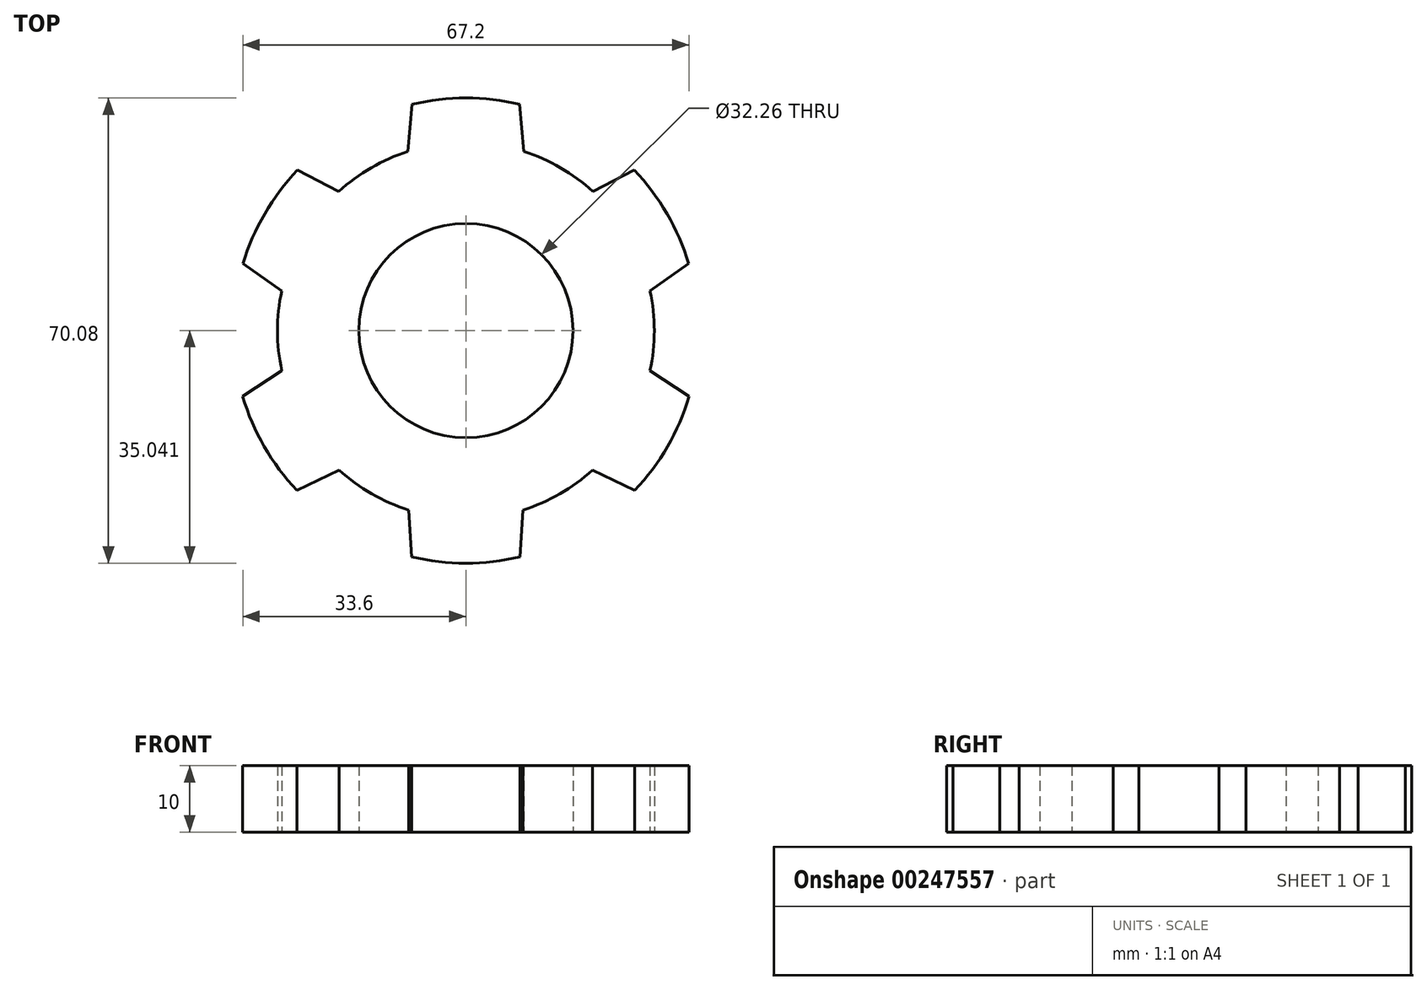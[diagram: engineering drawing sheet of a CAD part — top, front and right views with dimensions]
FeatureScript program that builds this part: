
annotation { "Feature Type Name" : "Feature", "Feature Type Description" : "" }
export const myFeature = defineFeature(function(context is Context, id is Id, definition is map)
    precondition{}
    {
        {
            var Q0;
            Q0=qCreatedBy(makeId("Top.planeOp"),FACE);
            var sketch = newSketch(context, id + "F0", { "sketchPlane" : qUnion([Q0])});
            skArc(sketch, "E0", {"start": v(-8.74, -1.22) * mm, "mid": v(-14.26, -3.69) * mm, "end": v(-19.13, -7.26) * mm});
            skArc(sketch, "E1", {"start": v(0, -63.26) * mm, "mid": v(4.11, -63.02) * mm, "end": v(8.17, -62.3) * mm});
            skLineSegment(sketch, "E2", {"start": v(8.1, 5.87) * mm, "end": v(8.74, -1.22) * mm});
            skLineSegment(sketch, "E3", {"start": v(25.36, -4.03) * mm, "end": v(19.13, -7.26) * mm});
            skLineSegment(sketch, "E4", {"start": v(33.56, -18.15) * mm, "end": v(27.74, -22.23) * mm});
            skLineSegment(sketch, "E5", {"start": v(33.6, -38.15) * mm, "end": v(27.72, -34.26) * mm});
            skPoint(sketch, "E6", {"position": v(25.45, -52.3) * mm});
            skPoint(sketch, "E7", {"position": v(19.08, -49.22) * mm});
            skLineSegment(sketch, "E8", {"start": v(19.08, -49.22) * mm, "end": v(25.45, -52.3) * mm});
            skLineSegment(sketch, "E9", {"start": v(8.62, -55.25) * mm, "end": v(8.17, -62.3) * mm});
            skArc(sketch, "E10.trimOffspring", {"start": v(8.1, 5.87) * mm, "mid": v(4.08, 6.58) * mm, "end": v(0, 6.82) * mm});
            skArc(sketch, "E11.trimOffspring", {"start": v(33.56, -18.15) * mm, "mid": v(30.3, -10.6) * mm, "end": v(25.36, -4.03) * mm});
            skArc(sketch, "E12.trimOffspring", {"start": v(25.45, -52.3) * mm, "mid": v(30.36, -45.71) * mm, "end": v(33.6, -38.15) * mm});
            skLineSegment(sketch, "E13.MirrorCS", {"start": v(-25.36, -4.03) * mm, "end": v(-19.13, -7.26) * mm});
            skPoint(sketch, "E14.MirrorP", {"position": v(-19.08, -49.22) * mm});
            skLineSegment(sketch, "E15.MirrorCS", {"start": v(-33.6, -38.15) * mm, "end": v(-27.72, -34.26) * mm});
            skPoint(sketch, "E16.MirrorP", {"position": v(-25.45, -52.3) * mm});
            skArc(sketch, "E17.MirrorCS", {"start": v(-25.45, -52.3) * mm, "mid": v(-30.36, -45.71) * mm, "end": v(-33.6, -38.15) * mm});
            skLineSegment(sketch, "E18.MirrorCS", {"start": v(-19.08, -49.22) * mm, "end": v(-25.45, -52.3) * mm});
            skLineSegment(sketch, "E19.MirrorCS", {"start": v(-8.1, 5.87) * mm, "end": v(-8.74, -1.22) * mm});
            skArc(sketch, "E20.MirrorCS", {"start": v(-33.56, -18.15) * mm, "mid": v(-30.3, -10.6) * mm, "end": v(-25.36, -4.03) * mm});
            skLineSegment(sketch, "E21.MirrorCS", {"start": v(-33.56, -18.15) * mm, "end": v(-27.74, -22.23) * mm});
            skLineSegment(sketch, "E22.MirrorCS", {"start": v(-8.62, -55.25) * mm, "end": v(-8.17, -62.3) * mm});
            skArc(sketch, "E23.MirrorC", {"start": v(8.74, -1.22) * mm, "mid": v(14.26, -3.69) * mm, "end": v(19.13, -7.26) * mm});
            skArc(sketch, "E24.MirrorCS", {"start": v(0, -63.26) * mm, "mid": v(-4.11, -63.02) * mm, "end": v(-8.17, -62.3) * mm});
            skArc(sketch, "E25.MirrorCS", {"start": v(-8.1, 5.87) * mm, "mid": v(-4.08, 6.58) * mm, "end": v(0, 6.82) * mm});
            skArc(sketch, "E26.trimOffspring", {"start": v(-27.74, -22.23) * mm, "mid": v(-28.37, -28.25) * mm, "end": v(-27.72, -34.26) * mm});
            skArc(sketch, "E27.trimOffspring", {"start": v(-19.13, -7.26) * mm, "mid": v(-14.26, -3.69) * mm, "end": v(-8.74, -1.22) * mm});
            skArc(sketch, "E28.trimOffspring", {"start": v(-27.72, -34.26) * mm, "mid": v(-28.37, -28.25) * mm, "end": v(-27.74, -22.23) * mm});
            skArc(sketch, "E29.trimOffspring", {"start": v(-19.08, -49.22) * mm, "mid": v(-14.18, -52.8) * mm, "end": v(-8.62, -55.25) * mm});
            skArc(sketch, "E30.trimOffspring", {"start": v(8.62, -55.25) * mm, "mid": v(14.18, -52.8) * mm, "end": v(19.08, -49.22) * mm});
            skArc(sketch, "E31.trimOffspring", {"start": v(-8.62, -55.25) * mm, "mid": v(-14.18, -52.8) * mm, "end": v(-19.08, -49.22) * mm});
            skArc(sketch, "E32.trimOffspring", {"start": v(19.08, -49.22) * mm, "mid": v(14.18, -52.8) * mm, "end": v(8.62, -55.25) * mm});
            skArc(sketch, "E33.trimOffspring", {"start": v(27.72, -34.26) * mm, "mid": v(28.37, -28.25) * mm, "end": v(27.74, -22.23) * mm});
            skArc(sketch, "E34.trimOffspring", {"start": v(19.13, -7.26) * mm, "mid": v(14.26, -3.69) * mm, "end": v(8.74, -1.22) * mm});
            skArc(sketch, "E35.trimOffspring", {"start": v(27.74, -22.23) * mm, "mid": v(28.37, -28.25) * mm, "end": v(27.72, -34.26) * mm});
            skCircle(sketch, "E36", {"center": v(0, -28.22) * mm, "radius": 16.13 * mm});
            skSolve(sketch);
        }
        {
            var Q0;
            Q0 = qSketchRegion(id + "F0", true);
            extrude(context, id + "F1", {"entities" : qUnion([Q0]), "depth" : 10 * mm});
        }
    });
